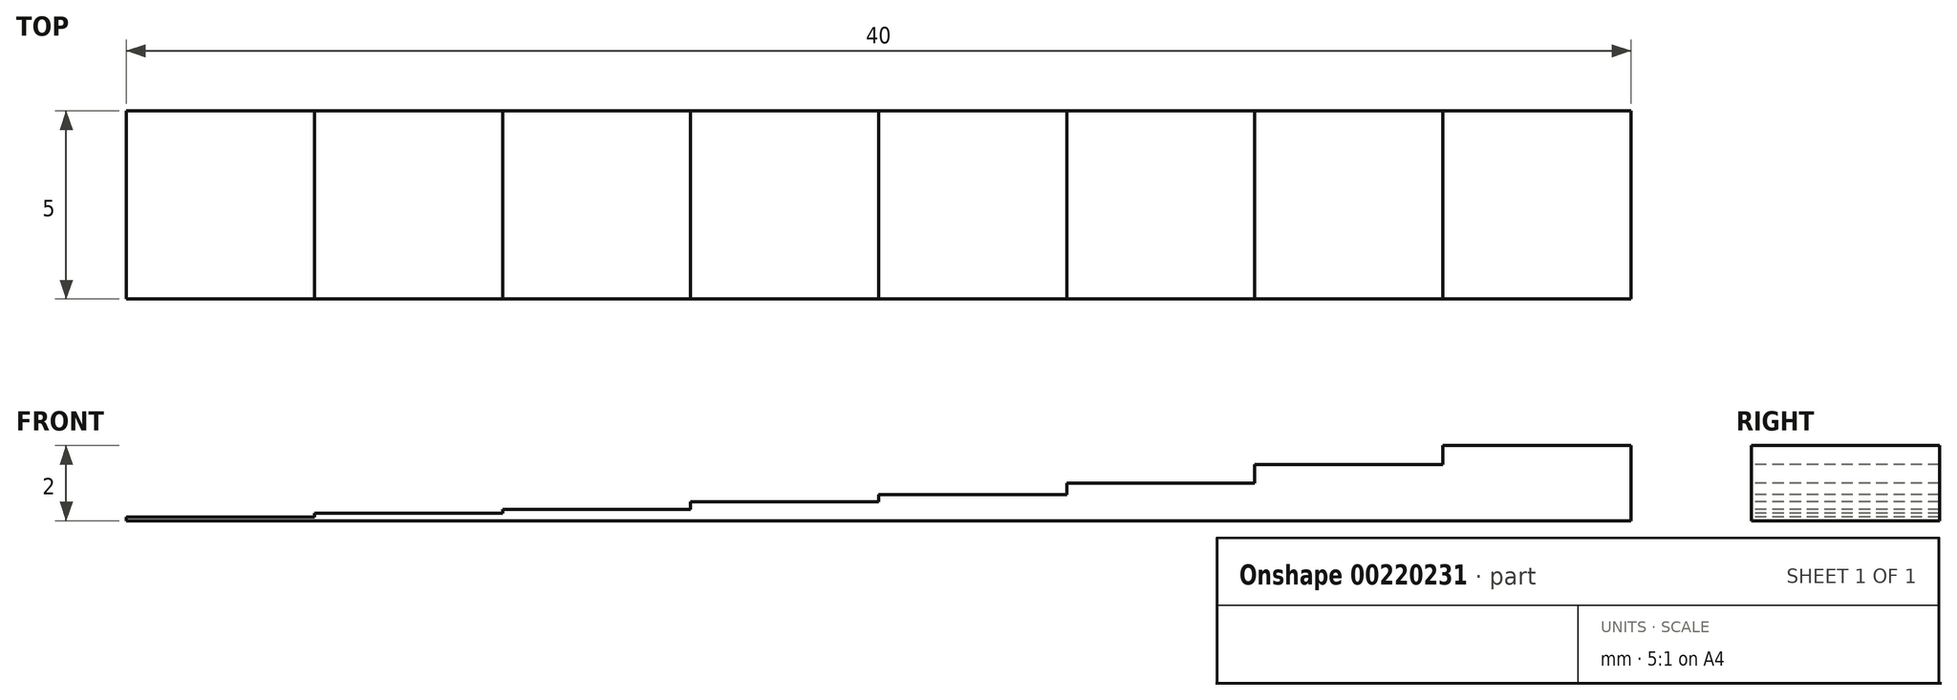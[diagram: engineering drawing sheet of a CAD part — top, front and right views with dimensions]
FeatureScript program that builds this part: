
annotation { "Feature Type Name" : "Feature", "Feature Type Description" : "" }
export const myFeature = defineFeature(function(context is Context, id is Id, definition is map)
    precondition{}
    {
        {
            var Q0;
            Q0=qCreatedBy(makeId("Top.planeOp"),FACE);
            var sketch = newSketch(context, id + "F0", { "sketchPlane" : qUnion([Q0])});
            skLineSegment(sketch, "E0.bottom", {"start": v(20, 2.5) * mm, "end": v(-20, 2.5) * mm});
            skLineSegment(sketch, "E0.top", {"start": v(20, -2.5) * mm, "end": v(-20, -2.5) * mm});
            skLineSegment(sketch, "E0.left", {"start": v(20, 2.5) * mm, "end": v(20, -2.5) * mm});
            skLineSegment(sketch, "E0.right", {"start": v(-20, 2.5) * mm, "end": v(-20, -2.5) * mm});
            skPoint(sketch, "E0.middle", {"position": v(0, 0) * mm});
            skLineSegment(sketch, "E1", {"start": v(-5, 2.5) * mm, "end": v(-5, -2.5) * mm});
            skLineSegment(sketch, "E2", {"start": v(0, 2.5) * mm, "end": v(0, -2.5) * mm});
            skLineSegment(sketch, "E3", {"start": v(5, 2.5) * mm, "end": v(5, -2.5) * mm});
            skLineSegment(sketch, "E4", {"start": v(10, 2.5) * mm, "end": v(10, -2.5) * mm});
            skLineSegment(sketch, "E5", {"start": v(15, 2.5) * mm, "end": v(15, -2.5) * mm});
            skLineSegment(sketch, "E6", {"start": v(-10, 2.5) * mm, "end": v(-10, -2.5) * mm});
            skLineSegment(sketch, "E7", {"start": v(-15, 2.5) * mm, "end": v(-15, -2.5) * mm});
            skSolve(sketch);
        }
        {
            var Q0;
            {var subQ0=sQuery(id+"F0.wireOp",EDGE,"E0.right");Q0=makeQuery(id+"F0.imprint","IMPRINT",FACE,{"disambiguationData":[TD([[makeQuery(id+"F0.imprint","IMPRINT",EDGE,{"derivedFrom":subQ0}),1.0]])]});}
            extrude(context, id + "F1", {"entities" : qUnion([Q0]), "depth" : 0.1 * mm});
        }
        {
            var Q0;
            {var subQ0=sQuery(id+"F0.wireOp",EDGE,"E1");Q0=makeQuery(id+"F0.imprint","IMPRINT",FACE,{"disambiguationData":[TD([[makeQuery(id+"F0.imprint","IMPRINT",EDGE,{"derivedFrom":subQ0}),1.0]])]});}
            extrude(context, id + "F2", {"entities" : qUnion([Q0]), "operationType" : NewBodyOperationType.ADD, "depth" : 0.5 * mm});
        }
        {
            var Q0;
            {var subQ0=sQuery(id+"F0.wireOp",EDGE,"E2");Q0=makeQuery(id+"F0.imprint","IMPRINT",FACE,{"disambiguationData":[TD([[makeQuery(id+"F0.imprint","IMPRINT",EDGE,{"derivedFrom":subQ0}),1.0]])]});}
            extrude(context, id + "F3", {"entities" : qUnion([Q0]), "operationType" : NewBodyOperationType.ADD, "depth" : 0.7 * mm});
        }
        {
            var Q0;
            {var subQ0=sQuery(id+"F0.wireOp",EDGE,"E3");Q0=makeQuery(id+"F0.imprint","IMPRINT",FACE,{"disambiguationData":[TD([[makeQuery(id+"F0.imprint","IMPRINT",EDGE,{"derivedFrom":subQ0}),1.0]])]});}
            extrude(context, id + "F4", {"entities" : qUnion([Q0]), "operationType" : NewBodyOperationType.ADD, "depth" : 1 * mm});
        }
        {
            var Q0;
            {var subQ0=sQuery(id+"F0.wireOp",EDGE,"E4");Q0=makeQuery(id+"F0.imprint","IMPRINT",FACE,{"disambiguationData":[TD([[makeQuery(id+"F0.imprint","IMPRINT",EDGE,{"derivedFrom":subQ0}),1.0]])]});}
            extrude(context, id + "F5", {"entities" : qUnion([Q0]), "operationType" : NewBodyOperationType.ADD, "depth" : 1.5 * mm});
        }
        {
            var Q0;
            {var subQ0=sQuery(id+"F0.wireOp",EDGE,"E0.left");Q0=makeQuery(id+"F0.imprint","IMPRINT",FACE,{"disambiguationData":[TD([[makeQuery(id+"F0.imprint","IMPRINT",EDGE,{"derivedFrom":subQ0}),-1.0]])]});}
            extrude(context, id + "F6", {"entities" : qUnion([Q0]), "operationType" : NewBodyOperationType.ADD, "depth" : 2 * mm});
        }
        {
            var Q0;
            {var subQ0=sQuery(id+"F0.wireOp",EDGE,"E6");Q0=makeQuery(id+"F0.imprint","IMPRINT",FACE,{"disambiguationData":[TD([[makeQuery(id+"F0.imprint","IMPRINT",EDGE,{"derivedFrom":subQ0}),-1.0]])]});}
            extrude(context, id + "F7", {"entities" : qUnion([Q0]), "operationType" : NewBodyOperationType.ADD, "depth" : 0.2 * mm});
        }
        {
            var Q0;
            {var subQ0=sQuery(id+"F0.wireOp",EDGE,"E1");Q0=makeQuery(id+"F0.imprint","IMPRINT",FACE,{"disambiguationData":[TD([[makeQuery(id+"F0.imprint","IMPRINT",EDGE,{"derivedFrom":subQ0}),-1.0]])]});}
            extrude(context, id + "F8", {"entities" : qUnion([Q0]), "operationType" : NewBodyOperationType.ADD, "depth" : 0.3 * mm});
        }
    });
